# Revit family: FH1 - 1300 bis 3000
name_source: partatom
category: HLS-Bauteile
revit_build: Autodesk Revit 2017 (Build: 20190507_1515(x64)
units: mm (PartAtom-declared; Revit-internal decimal feet)

## family parameters
Arbeitsebenenbasiert = Ja
Beim Laden mit Abzugskörper schneiden = Nein
Bemaßung runder Anschluss = Durchmesser verwenden
Gemeinsam genutzt = Ja
Immer vertikal = Nein
Raumberechnungspunkt = Nein
Teiletyp = Normal

## types (3) — shared parameters
Anschluss = M12
Breite = 80 mm  [stored 0.262467 ft]
Fabrikat = MEFA
Firma = MEFA Befestigungs- und Montagesysteme GmbH
Höhe = 130 mm
Länge = 60 mm  [stored 0.19685 ft]
Material = Stahl
Materialname = S235
Mengeneinheit = St
Oberflaeche = galvanisch verzinkt
Vorgabe-Ansicht = 1219 mm
min. Lastbereich = 0 N
vpe = 1 St

## per-type parameters (varying)
| type | Artikelnummer | EAN | Federrate | Gewicht | Gewicht pro Bauteil | Kurztext1 | Kurztext2 | max. Federweg | max. Lastbereich |
| Federhänger FH1 - 1300 | 0794130 | 4250928419118 | 41,58 N/mm | 0.95 kg | 0.95 kg | Federhänger FH 1 - 1300 | F 0 - 1.289 N max. Federweg 31 mm | 31 mm  [stored 0.101706 ft] | 1.289 N |
| Federhänger FH1 - 2100 | 0794210 | 4250928419125 | 75,46 N/mm | 1.15 kg | 1.15 kg | Federhänger FH 1 - 2100 | F 0 - 2.113 N max. Federweg 28 mm | 28 mm  [stored 0.0918635 ft] | 2.113 N |
| Federhänger FH1 - 3000 | 0794300 | 4250928419132 | 134,1 N/mm | 1.19 kg | 1.19 kg | Federhänger FH 1 - 3000 | F 0 - 3.084 N max. Federweg 23 mm | 23 mm  [stored 0.0754593 ft] | 3.084 N |

note: [stored X ft] marks values corroborated as IEEE doubles in the binary element streams (Revit-internal decimal feet)
